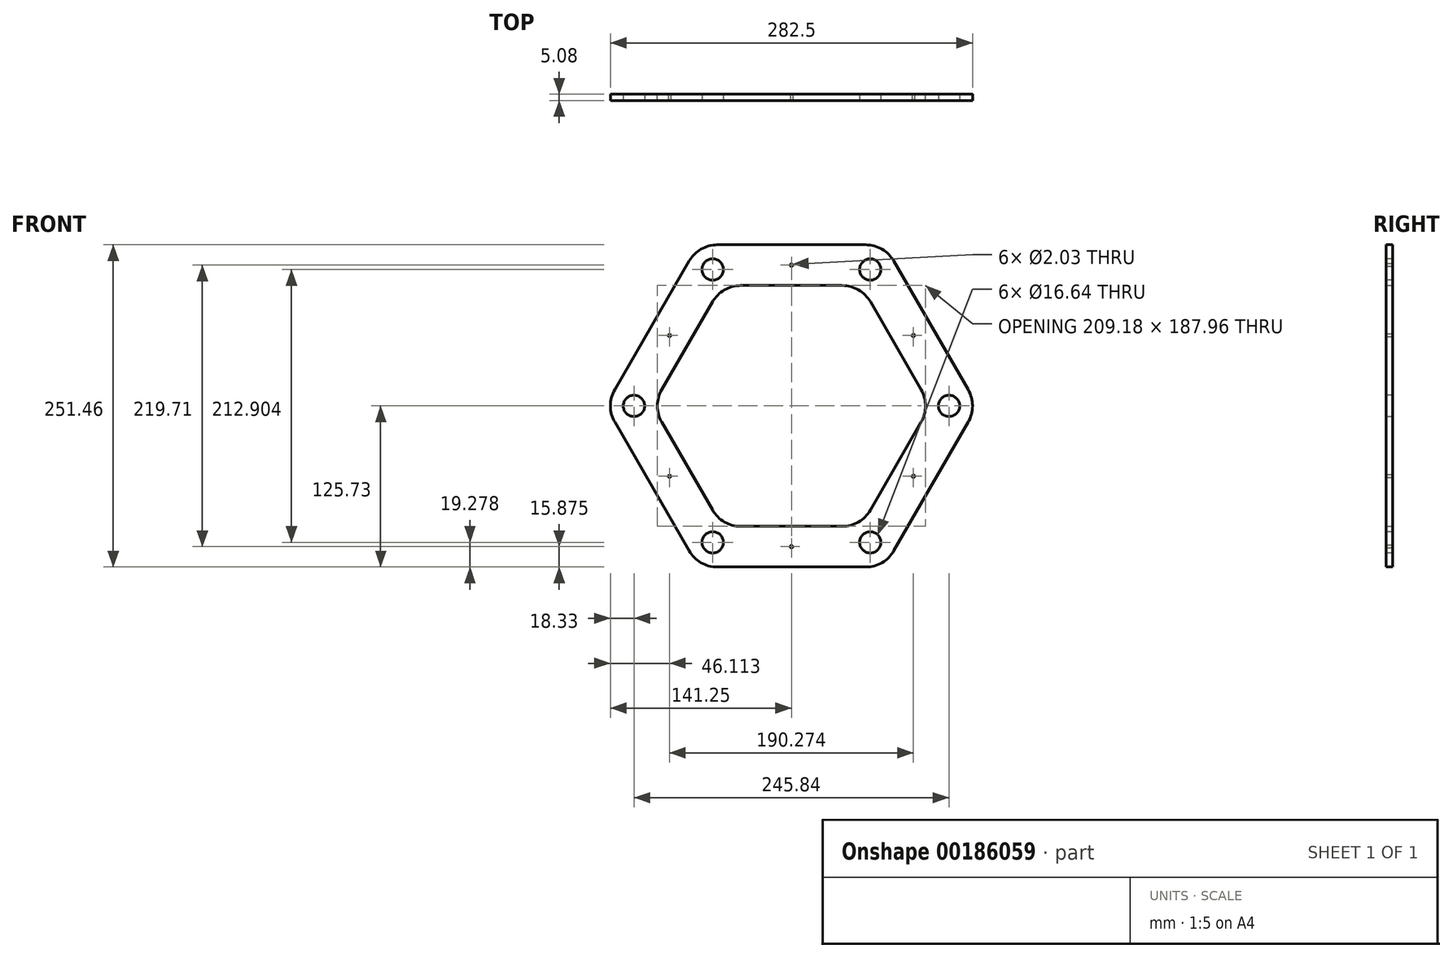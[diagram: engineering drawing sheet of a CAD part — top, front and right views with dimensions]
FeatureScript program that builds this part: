
annotation { "Feature Type Name" : "Feature", "Feature Type Description" : "" }
export const myFeature = defineFeature(function(context is Context, id is Id, definition is map)
    precondition{}
    {
        {
            var Q0;
            Q0=qCreatedBy(makeId("Front.planeOp"),FACE);
            var sketch = newSketch(context, id + "F0", { "sketchPlane" : qUnion([Q0])});
            skCircle(sketch, "E0.cCircle", {"center": v(0, 0) * mm, "radius": 125.73 * mm, "construction": true});
            skLineSegment(sketch, "E0.0", {"start": v(79.92, 113.03) * mm, "end": v(137.85, 12.7) * mm});
            skLineSegment(sketch, "E0.1", {"start": v(137.85, -12.7) * mm, "end": v(79.92, -113.03) * mm});
            skLineSegment(sketch, "E0.2", {"start": v(57.93, -125.73) * mm, "end": v(-57.93, -125.73) * mm});
            skLineSegment(sketch, "E0.3", {"start": v(-79.92, -113.03) * mm, "end": v(-137.85, -12.7) * mm});
            skLineSegment(sketch, "E0.4", {"start": v(-137.85, 12.7) * mm, "end": v(-79.92, 113.03) * mm});
            skLineSegment(sketch, "E0.5", {"start": v(-57.93, 125.73) * mm, "end": v(57.93, 125.73) * mm});
            skPoint(sketch, "E0.0.midPoint", {"position": v(108.89, 62.86) * mm});
            skCircle(sketch, "E1.cCircle", {"center": v(0, 0) * mm, "radius": 93.98 * mm, "construction": true});
            skLineSegment(sketch, "E1.0", {"start": v(-39.6, 93.98) * mm, "end": v(39.6, 93.98) * mm});
            skLineSegment(sketch, "E1.1", {"start": v(61.6, 81.28) * mm, "end": v(101.19, 12.7) * mm});
            skLineSegment(sketch, "E1.2", {"start": v(101.19, -12.7) * mm, "end": v(61.6, -81.28) * mm});
            skLineSegment(sketch, "E1.3", {"start": v(39.6, -93.98) * mm, "end": v(-39.6, -93.98) * mm});
            skLineSegment(sketch, "E1.4", {"start": v(-61.6, -81.28) * mm, "end": v(-101.19, -12.7) * mm});
            skLineSegment(sketch, "E1.5", {"start": v(-101.19, 12.7) * mm, "end": v(-61.6, 81.28) * mm});
            skPoint(sketch, "E1.0.midPoint", {"position": v(0, 93.98) * mm});
            skPoint(sketch, "E2.visualSharp", {"position": v(-72.6, 125.73) * mm});
            skArc(sketch, "E2.filletArc", {"start": v(-57.93, 125.73) * mm, "mid": v(-70.63, 122.33) * mm, "end": v(-79.92, 113.03) * mm});
            skPoint(sketch, "E3.visualSharp", {"position": v(72.6, 125.73) * mm});
            skArc(sketch, "E3.filletArc", {"start": v(79.92, 113.03) * mm, "mid": v(70.63, 122.33) * mm, "end": v(57.93, 125.73) * mm});
            skPoint(sketch, "E4.visualSharp", {"position": v(-145.18, 0) * mm});
            skArc(sketch, "E4.filletArc", {"start": v(-137.85, 12.7) * mm, "mid": v(-141.25, 0) * mm, "end": v(-137.85, -12.7) * mm});
            skPoint(sketch, "E5.visualSharp", {"position": v(145.18, 0) * mm});
            skArc(sketch, "E5.filletArc", {"start": v(137.85, -12.7) * mm, "mid": v(141.25, 0) * mm, "end": v(137.85, 12.7) * mm});
            skPoint(sketch, "E6.visualSharp", {"position": v(-72.6, -125.73) * mm});
            skArc(sketch, "E6.filletArc", {"start": v(-79.92, -113.03) * mm, "mid": v(-70.63, -122.33) * mm, "end": v(-57.93, -125.73) * mm});
            skPoint(sketch, "E7.visualSharp", {"position": v(72.6, -125.73) * mm});
            skArc(sketch, "E7.filletArc", {"start": v(57.93, -125.73) * mm, "mid": v(70.63, -122.33) * mm, "end": v(79.92, -113.03) * mm});
            skPoint(sketch, "E8.visualSharp", {"position": v(-54.26, 93.98) * mm});
            skArc(sketch, "E8.filletArc", {"start": v(-39.6, 93.98) * mm, "mid": v(-52.3, 90.58) * mm, "end": v(-61.6, 81.28) * mm});
            skPoint(sketch, "E9.visualSharp", {"position": v(54.26, 93.98) * mm});
            skArc(sketch, "E9.filletArc", {"start": v(61.6, 81.28) * mm, "mid": v(52.3, 90.58) * mm, "end": v(39.6, 93.98) * mm});
            skPoint(sketch, "E10.visualSharp", {"position": v(108.52, 0) * mm});
            skArc(sketch, "E10.filletArc", {"start": v(101.19, -12.7) * mm, "mid": v(104.59, 0) * mm, "end": v(101.19, 12.7) * mm});
            skPoint(sketch, "E11.visualSharp", {"position": v(54.26, -93.98) * mm});
            skArc(sketch, "E11.filletArc", {"start": v(39.6, -93.98) * mm, "mid": v(52.3, -90.58) * mm, "end": v(61.6, -81.28) * mm});
            skPoint(sketch, "E12.visualSharp", {"position": v(-54.26, -93.98) * mm});
            skArc(sketch, "E12.filletArc", {"start": v(-61.6, -81.28) * mm, "mid": v(-52.3, -90.58) * mm, "end": v(-39.6, -93.98) * mm});
            skPoint(sketch, "E13.visualSharp", {"position": v(-108.52, 0) * mm});
            skArc(sketch, "E13.filletArc", {"start": v(-101.19, 12.7) * mm, "mid": v(-104.59, 0) * mm, "end": v(-101.19, -12.7) * mm});
            skSolve(sketch);
        }
        {
            var Q0;
            Q0=makeQuery(id+"F0.imprint","IMPRINT",FACE,{"disambiguationData":[TD([[makeQuery(id+"F0.imprint","IMPRINT",EDGE,{"derivedFrom":sQuery(id+"F0.wireOp",EDGE,"E0.0")}),-1.0]])]});
            extrude(context, id + "F1", {"entities" : qUnion([Q0]), "depth" : 5.08 * mm});
        }
        {
            var Q0;
            Q0=makeQuery(id+"F1.opExtrude","CAP_FACE",FACE,{"disambiguationData":[OSD([sQuery(id+"F0.wireOp",EDGE,"E0.0"),sQuery(id+"F0.wireOp",EDGE,"E0.1"),sQuery(id+"F0.wireOp",EDGE,"E0.2"),sQuery(id+"F0.wireOp",EDGE,"E0.3"),sQuery(id+"F0.wireOp",EDGE,"E0.4"),sQuery(id+"F0.wireOp",EDGE,"E0.5"),sQuery(id+"F0.wireOp",EDGE,"E1.0"),sQuery(id+"F0.wireOp",EDGE,"E1.1"),sQuery(id+"F0.wireOp",EDGE,"E1.2"),sQuery(id+"F0.wireOp",EDGE,"E1.3"),sQuery(id+"F0.wireOp",EDGE,"E1.4"),sQuery(id+"F0.wireOp",EDGE,"E1.5"),sQuery(id+"F0.wireOp",EDGE,"E2.filletArc"),sQuery(id+"F0.wireOp",EDGE,"E3.filletArc"),sQuery(id+"F0.wireOp",EDGE,"E4.filletArc"),sQuery(id+"F0.wireOp",EDGE,"E5.filletArc"),sQuery(id+"F0.wireOp",EDGE,"E6.filletArc"),sQuery(id+"F0.wireOp",EDGE,"E7.filletArc"),sQuery(id+"F0.wireOp",EDGE,"E8.filletArc"),sQuery(id+"F0.wireOp",EDGE,"E9.filletArc"),sQuery(id+"F0.wireOp",EDGE,"E10.filletArc"),sQuery(id+"F0.wireOp",EDGE,"E11.filletArc"),sQuery(id+"F0.wireOp",EDGE,"E12.filletArc"),sQuery(id+"F0.wireOp",EDGE,"E13.filletArc")])],"isStart":false});
            var sketch = newSketch(context, id + "F2", { "sketchPlane" : qUnion([Q0])});
            skLineSegment(sketch, "E14", {"start": v(0, 0) * mm, "end": v(0, 109.86) * mm, "construction": true});
            skPoint(sketch, "E15", {"position": v(52.3, 90.58) * mm});
            skPoint(sketch, "E16", {"position": v(70.63, 122.33) * mm});
            skLineSegment(sketch, "E17", {"start": v(52.3, 90.58) * mm, "end": v(70.63, 122.33) * mm, "construction": true});
            skPoint(sketch, "E18", {"position": v(61.46, 106.45) * mm});
            skCircle(sketch, "E19", {"center": v(0, 109.86) * mm, "radius": 1.02 * mm});
            skCircle(sketch, "E20", {"center": v(61.46, 106.45) * mm, "radius": 8.32 * mm});
            skCircle(sketch, "E21.1.0", {"center": v(-61.46, 106.45) * mm, "radius": 8.32 * mm});
            skCircle(sketch, "E21.2.0", {"center": v(-122.92, 0) * mm, "radius": 8.32 * mm});
            skCircle(sketch, "E21.3.0", {"center": v(-61.46, -106.45) * mm, "radius": 8.32 * mm});
            skCircle(sketch, "E21.4.0", {"center": v(61.46, -106.45) * mm, "radius": 8.32 * mm});
            skCircle(sketch, "E21.5.0", {"center": v(122.92, 0) * mm, "radius": 8.32 * mm});
            skPoint(sketch, "E21.center", {"position": v(0, 0) * mm});
            skCircle(sketch, "E22.1.0", {"center": v(-95.14, 54.93) * mm, "radius": 1.02 * mm});
            skCircle(sketch, "E22.2.0", {"center": v(-95.14, -54.93) * mm, "radius": 1.02 * mm});
            skCircle(sketch, "E22.3.0", {"center": v(0, -109.86) * mm, "radius": 1.02 * mm});
            skCircle(sketch, "E22.4.0", {"center": v(95.14, -54.93) * mm, "radius": 1.02 * mm});
            skCircle(sketch, "E22.5.0", {"center": v(95.14, 54.93) * mm, "radius": 1.02 * mm});
            skSolve(sketch);
        }
        {
            var Q0;
            Q0=makeQuery(id+"F2.imprint","IMPRINT",FACE,{"disambiguationData":[TD([[makeQuery(id+"F2.imprint","IMPRINT",EDGE,{"derivedFrom":sQuery(id+"F2.wireOp",EDGE,"E19")}),1.0]])]});
            var Q1;
            Q1=makeQuery(id+"F2.imprint","IMPRINT",FACE,{"disambiguationData":[TD([[makeQuery(id+"F2.imprint","IMPRINT",EDGE,{"derivedFrom":sQuery(id+"F2.wireOp",EDGE,"E22.1.0")}),1.0]])]});
            var Q2;
            Q2=makeQuery(id+"F2.imprint","IMPRINT",FACE,{"disambiguationData":[TD([[makeQuery(id+"F2.imprint","IMPRINT",EDGE,{"derivedFrom":sQuery(id+"F2.wireOp",EDGE,"E22.2.0")}),1.0]])]});
            var Q3;
            Q3=makeQuery(id+"F2.imprint","IMPRINT",FACE,{"disambiguationData":[TD([[makeQuery(id+"F2.imprint","IMPRINT",EDGE,{"derivedFrom":sQuery(id+"F2.wireOp",EDGE,"E22.3.0")}),1.0]])]});
            var Q4;
            Q4=makeQuery(id+"F2.imprint","IMPRINT",FACE,{"disambiguationData":[TD([[makeQuery(id+"F2.imprint","IMPRINT",EDGE,{"derivedFrom":sQuery(id+"F2.wireOp",EDGE,"E22.4.0")}),1.0]])]});
            var Q5;
            Q5=makeQuery(id+"F2.imprint","IMPRINT",FACE,{"disambiguationData":[TD([[makeQuery(id+"F2.imprint","IMPRINT",EDGE,{"derivedFrom":sQuery(id+"F2.wireOp",EDGE,"E22.5.0")}),1.0]])]});
            extrude(context, id + "F3", {"entities" : qUnion([Q0, Q1, Q2, Q3, Q4, Q5]), "operationType" : NewBodyOperationType.REMOVE, "endBound" : BoundingType.THROUGH_ALL, "oppositeDirection" : true, "depth" : 25.4 * mm});
        }
        {
            var Q0;
            Q0=makeQuery(id+"F2.imprint","IMPRINT",FACE,{"disambiguationData":[TD([[makeQuery(id+"F2.imprint","IMPRINT",EDGE,{"derivedFrom":sQuery(id+"F2.wireOp",EDGE,"E21.1.0")}),1.0]])]});
            var Q1;
            Q1=makeQuery(id+"F2.imprint","IMPRINT",FACE,{"disambiguationData":[TD([[makeQuery(id+"F2.imprint","IMPRINT",EDGE,{"derivedFrom":sQuery(id+"F2.wireOp",EDGE,"E20")}),1.0]])]});
            var Q2;
            Q2=makeQuery(id+"F2.imprint","IMPRINT",FACE,{"disambiguationData":[TD([[makeQuery(id+"F2.imprint","IMPRINT",EDGE,{"derivedFrom":sQuery(id+"F2.wireOp",EDGE,"E21.5.0")}),1.0]])]});
            var Q3;
            Q3=makeQuery(id+"F2.imprint","IMPRINT",FACE,{"disambiguationData":[TD([[makeQuery(id+"F2.imprint","IMPRINT",EDGE,{"derivedFrom":sQuery(id+"F2.wireOp",EDGE,"E21.4.0")}),1.0]])]});
            var Q4;
            Q4=makeQuery(id+"F2.imprint","IMPRINT",FACE,{"disambiguationData":[TD([[makeQuery(id+"F2.imprint","IMPRINT",EDGE,{"derivedFrom":sQuery(id+"F2.wireOp",EDGE,"E21.3.0")}),1.0]])]});
            var Q5;
            Q5=makeQuery(id+"F2.imprint","IMPRINT",FACE,{"disambiguationData":[TD([[makeQuery(id+"F2.imprint","IMPRINT",EDGE,{"derivedFrom":sQuery(id+"F2.wireOp",EDGE,"E21.2.0")}),1.0]])]});
            extrude(context, id + "F4", {"entities" : qUnion([Q0, Q1, Q2, Q3, Q4, Q5]), "operationType" : NewBodyOperationType.REMOVE, "endBound" : BoundingType.THROUGH_ALL, "oppositeDirection" : true, "depth" : 2.54 * mm});
        }
    });
